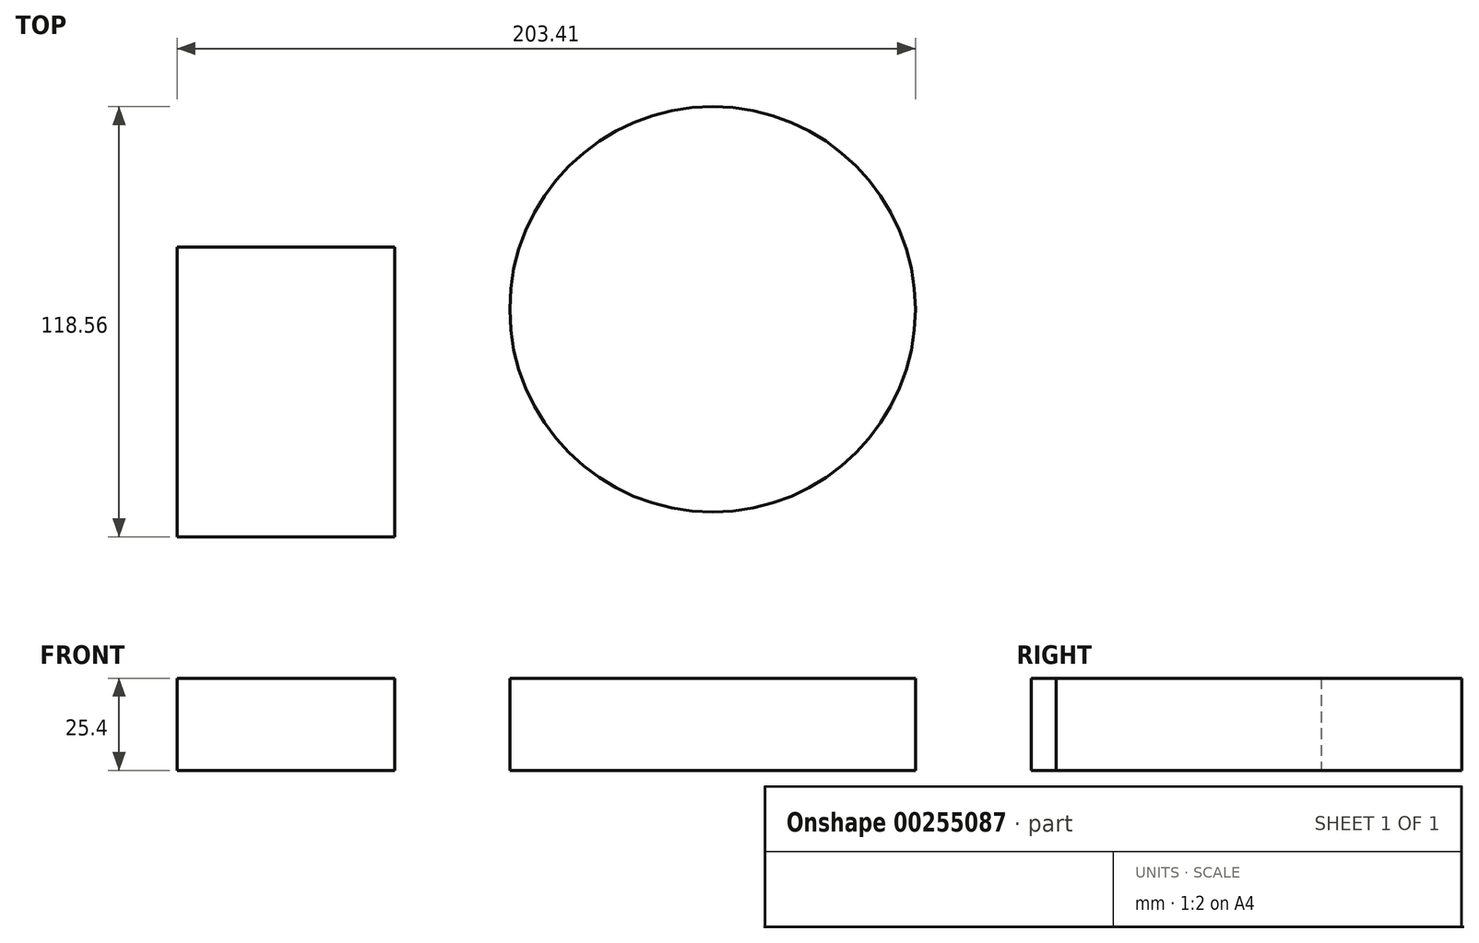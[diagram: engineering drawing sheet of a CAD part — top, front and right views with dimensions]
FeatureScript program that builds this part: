
annotation { "Feature Type Name" : "Feature", "Feature Type Description" : "" }
export const myFeature = defineFeature(function(context is Context, id is Id, definition is map)
    precondition{}
    {
        {
            var Q0;
            Q0=qCreatedBy(makeId("Top.planeOp"),FACE);
            var sketch = newSketch(context, id + "F0", { "sketchPlane" : qUnion([Q0])});
            skLineSegment(sketch, "E0.bottom", {"start": v(-136.1, 35.92) * mm, "end": v(-76.1, 35.92) * mm});
            skLineSegment(sketch, "E0.top", {"start": v(-136.1, -43.94) * mm, "end": v(-76.1, -43.94) * mm});
            skLineSegment(sketch, "E0.left", {"start": v(-136.1, 35.92) * mm, "end": v(-136.1, -43.94) * mm});
            skLineSegment(sketch, "E0.right", {"start": v(-76.1, 35.92) * mm, "end": v(-76.1, -43.94) * mm});
            skCircle(sketch, "E1", {"center": v(11.44, 18.75) * mm, "radius": 55.88 * mm});
            skSolve(sketch);
        }
        {
            var Q0;
            Q0 = qSketchRegion(id + "F0", true);
            extrude(context, id + "F1", {"entities" : qUnion([Q0]), "depth" : 25.4 * mm});
        }
    });
